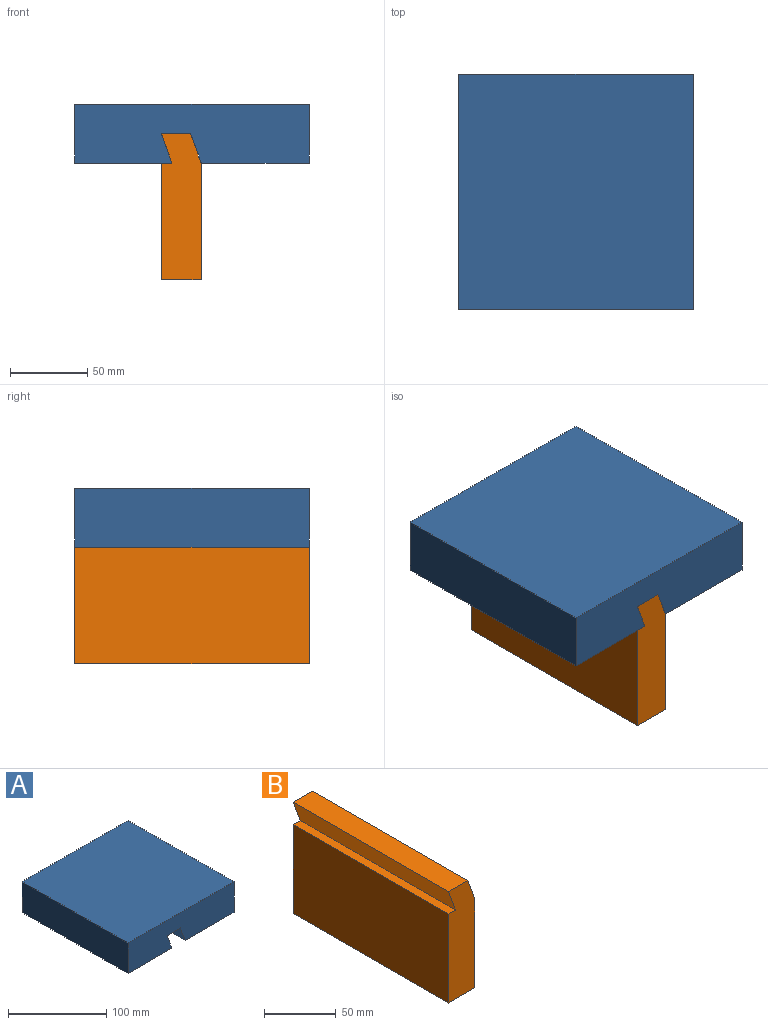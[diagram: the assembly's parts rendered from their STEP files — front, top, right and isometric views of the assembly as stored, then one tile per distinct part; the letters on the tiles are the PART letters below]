
ASSEMBLY  parts=2 mates=1
PART A: 10 faces, bbox 152.4x152.4x38.1 mm
  f0: plane 152.4x19.05mm, normal (0.94,0,0.34), area 3089.5mm2, adj f1,f7,f8,f9
  f1: plane 152.4x19.05mm, normal (0,0,-1), area 2903.2mm2, adj f0,f2,f8,f9
  f2: plane 152.4x19.05mm, normal (-0.94,0,-0.35), area 3097.7mm2, adj f1,f3,f8,f9
  f3: plane 152.4x70.07mm, normal (0,0,-1), area 10679mm2, adj f2,f4,f8,f9
  f4: plane 152.4x38.1mm, normal (1,0,0), area 5806.4mm2, adj f3,f5,f8,f9
  f5: plane 152.4x152.4mm, normal (0,0,1), area 23225.8mm2, adj f4,f6,f8,f9
  f6: plane 152.4x38.1mm, normal (-1,0,0), area 5806.4mm2, adj f5,f7,f8,f9
  f7: plane 152.4x63.12mm, normal (0,0,-1), area 9619.8mm2, adj f0,f6,f8,f9
  f8: plane 152.4x38.1mm, normal (0,-1,0), area 5442.1mm2, adj f0,f1,f2,f3,f4,f5,f6,f7
  f9: plane 152.4x38.1mm, normal (0,1,0), area 5442.1mm2, adj f0,f1,f2,f3,f4,f5,f6,f7
PART B: 9 faces, bbox 25.9x152.4x94.7 mm
  f0: plane 152.4x75.64mm, normal (1,0,0), area 11527.8mm2, adj f1,f6,f7,f8
  f1: plane 152.4x19.05mm, normal (0.94,0,0.34), area 3089.5mm2, adj f0,f2,f7,f8
  f2: plane 152.4x18.97mm, normal (0,0,1), area 2891.7mm2, adj f1,f3,f7,f8
  f3: plane 152.4x19.05mm, normal (-0.94,0,-0.34), area 3089.5mm2, adj f2,f4,f7,f8
  f4: plane 152.4x6.93mm, normal (0,0,1), area 1056.7mm2, adj f3,f5,f7,f8
  f5: plane 152.4x75.64mm, normal (-1,0,0), area 11527.8mm2, adj f4,f6,f7,f8
  f6: plane 152.4x25.91mm, normal (0,0,-1), area 3948.4mm2, adj f0,f5,f7,f8
  f7: plane 94.69x25.91mm, normal (0,-1,0), area 2321.2mm2, adj f0,f1,f2,f3,f4,f5,f6
  f8: plane 94.69x25.91mm, normal (0,1,0), area 2321.2mm2, adj f0,f1,f2,f3,f4,f5,f6
PLACE A t=(6.71,0,-53.11)mm
PLACE B t=(6.71,0,32.02)mm
MATE fastened B.f7 <-> A.f8  axis (0,-1,0) through (6.71,-152.4,-60.48)mm
